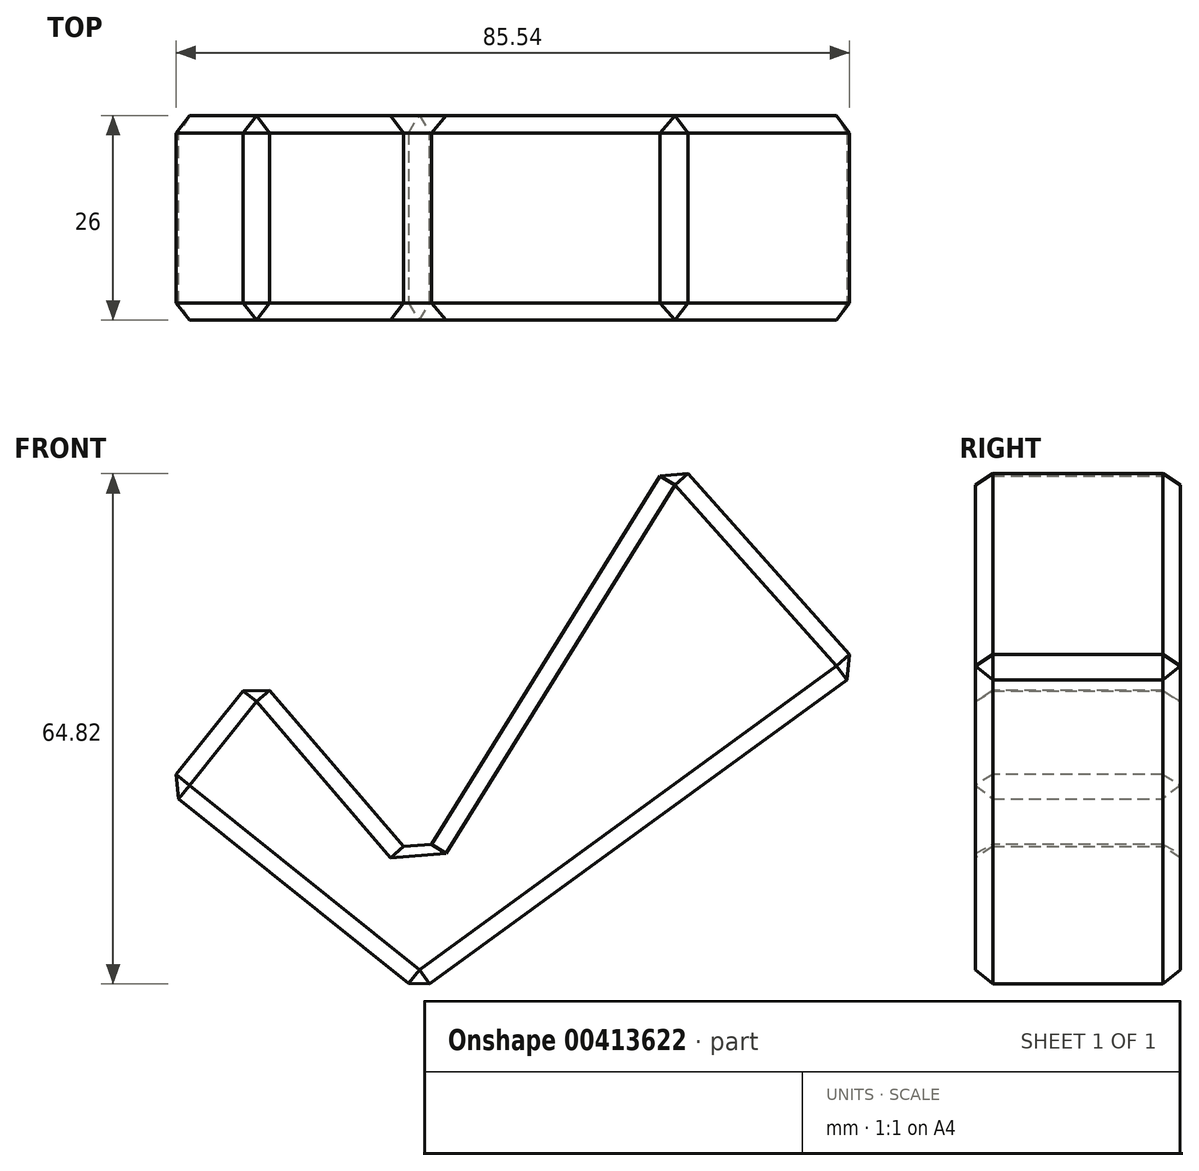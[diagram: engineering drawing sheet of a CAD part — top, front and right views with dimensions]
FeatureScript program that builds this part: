
annotation { "Feature Type Name" : "Feature", "Feature Type Description" : "" }
export const myFeature = defineFeature(function(context is Context, id is Id, definition is map)
    precondition{}
    {
        {
            var Q0;
            Q0=qCreatedBy(makeId("Front.planeOp"),FACE);
            var sketch = newSketch(context, id + "F0", { "sketchPlane" : qUnion([Q0])});
            skLineSegment(sketch, "E0", {"start": v(-32.2, 15.11) * mm, "end": v(-20.7, 29.5) * mm});
            skLineSegment(sketch, "E1", {"start": v(-20.7, 29.5) * mm, "end": v(0, 5.4) * mm});
            skLineSegment(sketch, "E2", {"start": v(0, 5.4) * mm, "end": v(32.2, 57.22) * mm});
            skLineSegment(sketch, "E3", {"start": v(32.2, 57.22) * mm, "end": v(56.32, 30.23) * mm});
            skLineSegment(sketch, "E4", {"start": v(56.32, 30.23) * mm, "end": v(0, -10.8) * mm});
            skLineSegment(sketch, "E5", {"start": v(0, -10.8) * mm, "end": v(-32.2, 15.11) * mm});
            skSolve(sketch);
        }
        {
            var Q0;
            Q0 = qSketchRegion(id + "F0", true);
            extrude(context, id + "F1", {"entities" : qUnion([Q0]), "endBound" : BoundingType.SYMMETRIC, "offsetDistance" : 25 * mm, "depth" : 26 * mm});
        }
        {
            var Q0;
            Q0=makeQuery(id+"F1.opExtrude","SWEPT_EDGE",EDGE,{"disambiguationData":[OSD([sQuery(id+"F0.wireOp",EDGE,"E1"),sQuery(id+"F0.wireOp",EDGE,"E2")])]});
            var Q1;
            Q1=makeQuery(id+"F1.opExtrude","SWEPT_EDGE",EDGE,{"disambiguationData":[OSD([sQuery(id+"F0.wireOp",EDGE,"E3"),sQuery(id+"F0.wireOp",EDGE,"E4")])]});
            var Q2;
            Q2=makeQuery(id+"F1.opExtrude","SWEPT_EDGE",EDGE,{"disambiguationData":[OSD([sQuery(id+"F0.wireOp",EDGE,"E0"),sQuery(id+"F0.wireOp",EDGE,"E1")])]});
            var Q3;
            Q3=makeQuery(id+"F1.opExtrude","SWEPT_EDGE",EDGE,{"disambiguationData":[OSD([sQuery(id+"F0.wireOp",EDGE,"E0"),sQuery(id+"F0.wireOp",EDGE,"E5")])]});
            var Q4;
            Q4=makeQuery(id+"F1.opExtrude","CAP_EDGE",EDGE,{"disambiguationData":[OSD([sQuery(id+"F0.wireOp",EDGE,"E4")])],"isStart":false});
            var Q5;
            Q5=makeQuery(id+"F1.opExtrude","SWEPT_EDGE",EDGE,{"disambiguationData":[OSD([sQuery(id+"F0.wireOp",EDGE,"E2"),sQuery(id+"F0.wireOp",EDGE,"E3")])]});
            var Q6;
            Q6=makeQuery(id+"F1.opExtrude","CAP_EDGE",EDGE,{"disambiguationData":[OSD([sQuery(id+"F0.wireOp",EDGE,"E3")])],"isStart":false});
            var Q7;
            Q7=makeQuery(id+"F1.opExtrude","CAP_EDGE",EDGE,{"disambiguationData":[OSD([sQuery(id+"F0.wireOp",EDGE,"E0")])],"isStart":true});
            var Q8;
            Q8=makeQuery(id+"F1.opExtrude","CAP_EDGE",EDGE,{"disambiguationData":[OSD([sQuery(id+"F0.wireOp",EDGE,"E0")])],"isStart":false});
            var Q9;
            Q9=makeQuery(id+"F1.opExtrude","CAP_EDGE",EDGE,{"disambiguationData":[OSD([sQuery(id+"F0.wireOp",EDGE,"E1")])],"isStart":true});
            var Q10;
            Q10=makeQuery(id+"F1.opExtrude","CAP_EDGE",EDGE,{"disambiguationData":[OSD([sQuery(id+"F0.wireOp",EDGE,"E2")])],"isStart":true});
            var Q11;
            Q11=makeQuery(id+"F1.opExtrude","CAP_EDGE",EDGE,{"disambiguationData":[OSD([sQuery(id+"F0.wireOp",EDGE,"E2")])],"isStart":false});
            var Q12;
            Q12=makeQuery(id+"F1.opExtrude","CAP_EDGE",EDGE,{"disambiguationData":[OSD([sQuery(id+"F0.wireOp",EDGE,"E3")])],"isStart":true});
            var Q13;
            Q13=makeQuery(id+"F1.opExtrude","CAP_EDGE",EDGE,{"disambiguationData":[OSD([sQuery(id+"F0.wireOp",EDGE,"E5")])],"isStart":false});
            var Q14;
            Q14=makeQuery(id+"F1.opExtrude","CAP_EDGE",EDGE,{"disambiguationData":[OSD([sQuery(id+"F0.wireOp",EDGE,"E4")])],"isStart":true});
            var Q15;
            Q15=makeQuery(id+"F1.opExtrude","SWEPT_EDGE",EDGE,{"disambiguationData":[OSD([sQuery(id+"F0.wireOp",EDGE,"E4"),sQuery(id+"F0.wireOp",EDGE,"E5")])]});
            var Q16;
            Q16=makeQuery(id+"F1.opExtrude","CAP_EDGE",EDGE,{"disambiguationData":[OSD([sQuery(id+"F0.wireOp",EDGE,"E1")])],"isStart":false});
            var Q17;
            Q17=makeQuery(id+"F1.opExtrude","CAP_EDGE",EDGE,{"disambiguationData":[OSD([sQuery(id+"F0.wireOp",EDGE,"E5")])],"isStart":true});
            chamfer(context, id + "F2", {"entities" : qUnion([Q0, Q1, Q2, Q3, Q4, Q5, Q6, Q7, Q8, Q9, Q10, Q11, Q12, Q13, Q14, Q15, Q16, Q17]), "width" : 2.2 * mm, "tangentPropagation" : true});
        }
    });
